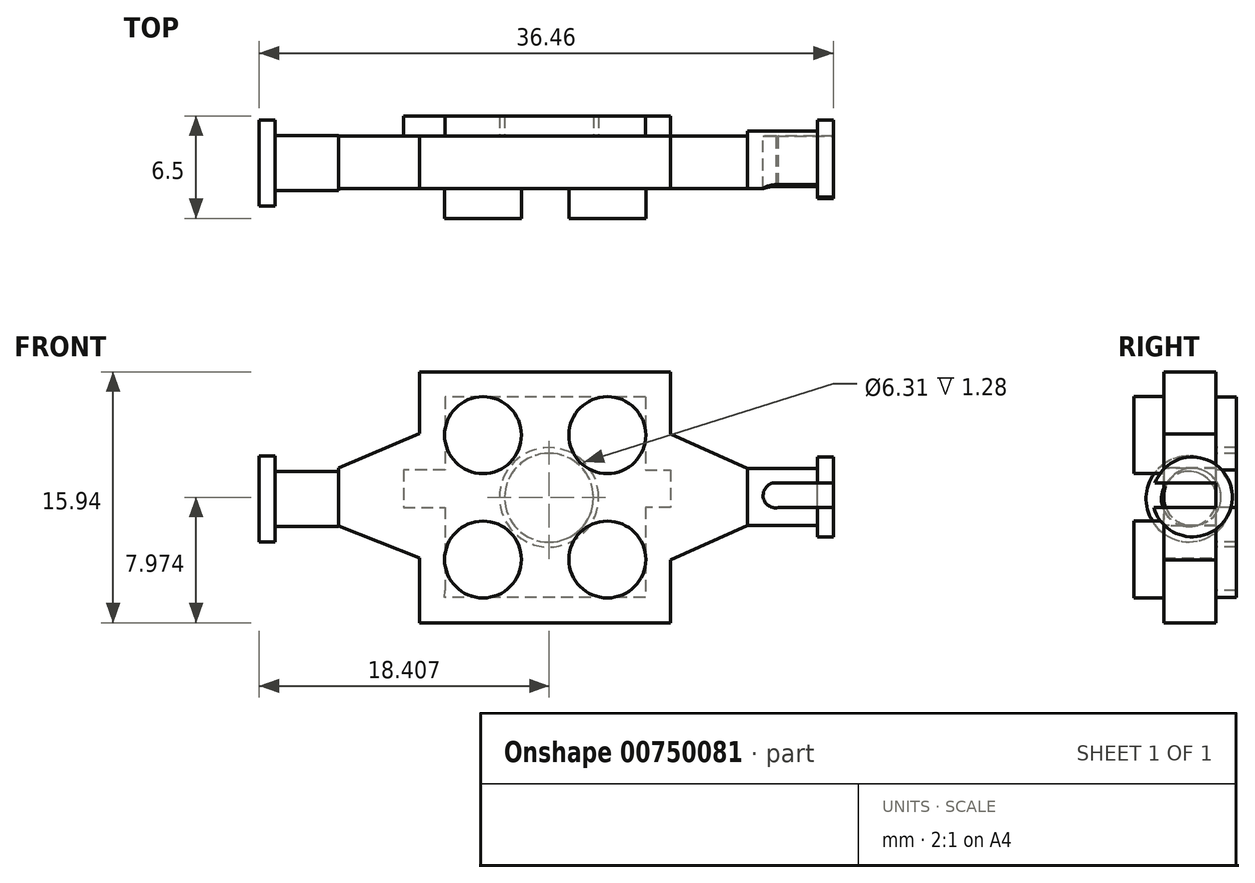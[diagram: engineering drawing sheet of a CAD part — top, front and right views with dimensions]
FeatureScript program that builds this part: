
annotation { "Feature Type Name" : "Feature", "Feature Type Description" : "" }
export const myFeature = defineFeature(function(context is Context, id is Id, definition is map)
    precondition{}
    {
        {
            var Q0;
            Q0=qCreatedBy(makeId("Front.planeOp"),FACE);
            var sketch = newSketch(context, id + "F0", { "sketchPlane" : qUnion([Q0])});
            skLineSegment(sketch, "E0.bottom", {"start": v(-41.3, 42.7) * mm, "end": v(-25.36, 42.7) * mm});
            skLineSegment(sketch, "E0.top", {"start": v(-41.3, 26.75) * mm, "end": v(-25.36, 26.75) * mm});
            skLineSegment(sketch, "E0.left", {"start": v(-41.3, 42.7) * mm, "end": v(-41.3, 26.75) * mm});
            skLineSegment(sketch, "E0.right", {"start": v(-25.36, 42.7) * mm, "end": v(-25.36, 26.75) * mm});
            skSolve(sketch);
        }
        {
            var Q0;
            Q0=makeQuery(id+"F0.imprint","IMPRINT",FACE,{"disambiguationData":[TD([[makeQuery(id+"F0.imprint","IMPRINT",EDGE,{"derivedFrom":sQuery(id+"F0.wireOp",EDGE,"E0.bottom")}),-1.0]])]});
            extrude(context, id + "F1", {"entities" : qUnion([Q0]), "depth" : 3.32 * mm, "offsetDistance" : 25 * mm});
        }
        {
            var Q0;
            Q0=makeQuery(id+"F1.opExtrude","CAP_FACE",FACE,{"disambiguationData":[OSD([sQuery(id+"F0.wireOp",EDGE,"E0.bottom"),sQuery(id+"F0.wireOp",EDGE,"E0.top"),sQuery(id+"F0.wireOp",EDGE,"E0.left"),sQuery(id+"F0.wireOp",EDGE,"E0.right")])],"isStart":false});
            var sketch = newSketch(context, id + "F2", { "sketchPlane" : qUnion([Q0])});
            skCircle(sketch, "E1", {"center": v(-37.28, 38.67) * mm, "radius": 2.44 * mm});
            skCircle(sketch, "E2", {"center": v(-29.38, 38.67) * mm, "radius": 2.44 * mm});
            skCircle(sketch, "E3", {"center": v(-37.28, 30.77) * mm, "radius": 2.44 * mm});
            skCircle(sketch, "E4", {"center": v(-29.38, 30.77) * mm, "radius": 2.44 * mm});
            skLineSegment(sketch, "E5", {"start": v(-26.94, 38.67) * mm, "end": v(-25.36, 38.67) * mm});
            skLineSegment(sketch, "E6", {"start": v(-29.38, 41.11) * mm, "end": v(-29.38, 42.7) * mm});
            skLineSegment(sketch, "E7", {"start": v(-39.72, 38.67) * mm, "end": v(-41.3, 38.67) * mm});
            skLineSegment(sketch, "E8", {"start": v(-37.28, 41.11) * mm, "end": v(-37.28, 42.7) * mm});
            skLineSegment(sketch, "E9", {"start": v(-39.72, 30.77) * mm, "end": v(-41.3, 30.77) * mm});
            skLineSegment(sketch, "E10", {"start": v(-37.28, 28.33) * mm, "end": v(-37.28, 26.75) * mm});
            skLineSegment(sketch, "E11", {"start": v(-29.38, 28.33) * mm, "end": v(-29.38, 26.75) * mm});
            skLineSegment(sketch, "E12", {"start": v(-26.94, 30.77) * mm, "end": v(-25.36, 30.77) * mm});
            skSolve(sketch);
        }
        {
            var Q0;
            Q0 = qSketchRegion(id + "F2", true);
            extrude(context, id + "F3", {"entities" : qUnion([Q0]), "operationType" : NewBodyOperationType.ADD, "depth" : 1.9 * mm, "offsetDistance" : 25 * mm});
        }
        {
            var Q0;
            Q0=makeQuery(id+"F1.opExtrude","CAP_FACE",FACE,{"disambiguationData":[OSD([sQuery(id+"F0.wireOp",EDGE,"E0.bottom"),sQuery(id+"F0.wireOp",EDGE,"E0.top"),sQuery(id+"F0.wireOp",EDGE,"E0.left"),sQuery(id+"F0.wireOp",EDGE,"E0.right")])],"isStart":false});
            var sketch = newSketch(context, id + "F4", { "sketchPlane" : qUnion([Q0])});
            skLineSegment(sketch, "E13", {"start": v(-25.36, 38.73) * mm, "end": v(-20.49, 36.54) * mm});
            skLineSegment(sketch, "E14", {"start": v(-20.49, 36.54) * mm, "end": v(-20.49, 32.95) * mm});
            skLineSegment(sketch, "E15", {"start": v(-20.49, 32.95) * mm, "end": v(-25.36, 30.76) * mm});
            skLineSegment(sketch, "E16", {"start": v(-25.36, 30.76) * mm, "end": v(-25.36, 38.73) * mm});
            skSolve(sketch);
        }
        {
            var Q0;
            Q0 = qSketchRegion(id + "F4", true);
            extrude(context, id + "F5", {"entities" : qUnion([Q0]), "oppositeDirection" : true, "depth" : 3.32 * mm, "offsetDistance" : 25 * mm});
        }
        {
            var Q0;
            Q0=makeQuery(id+"F5.opExtrude","SWEPT_FACE",FACE,{"disambiguationData":[OSD([sQuery(id+"F4.wireOp",EDGE,"E14")])]});
            var sketch = newSketch(context, id + "F6", { "sketchPlane" : qUnion([Q0])});
            skCircle(sketch, "E17", {"center": v(-1.5, 34.75) * mm, "radius": 1.82 * mm});
            skPoint(sketch, "E17.centerSnap0", {"position": v(0, 34.75) * mm});
            skSolve(sketch);
        }
        {
            var Q0;
            Q0 = qSketchRegion(id + "F6", true);
            extrude(context, id + "F7", {"entities" : qUnion([Q0]), "operationType" : NewBodyOperationType.ADD, "depth" : 4.44 * mm, "offsetDistance" : 25 * mm});
        }
        {
            var Q0;
            Q0=makeQuery(id+"F7.opExtrude","CAP_FACE",FACE,{"disambiguationData":[OSD([sQuery(id+"F6.wireOp",EDGE,"E17")])],"isStart":false});
            var sketch = newSketch(context, id + "F8", { "sketchPlane" : qUnion([Q0])});
            skCircle(sketch, "E18", {"center": v(-1.5, 34.75) * mm, "radius": 2.54 * mm});
            skSolve(sketch);
        }
        {
            var Q0;
            Q0 = qSketchRegion(id + "F8", true);
            extrude(context, id + "F9", {"entities" : qUnion([Q0]), "operationType" : NewBodyOperationType.ADD, "depth" : 1.02 * mm, "offsetDistance" : 25 * mm});
        }
        {
            var Q0;
            Q0=qCreatedBy(makeId("Front.planeOp"),FACE);
            var sketch = newSketch(context, id + "F10", { "sketchPlane" : qUnion([Q0])});
            skArc(sketch, "E19", {"start": v(-18.64, 35.65) * mm, "mid": v(-19.49, 34.79) * mm, "end": v(-18.52, 34.07) * mm});
            skLineSegment(sketch, "E20", {"start": v(-18.64, 35.65) * mm, "end": v(-15.04, 35.65) * mm});
            skLineSegment(sketch, "E21", {"start": v(-15.04, 35.65) * mm, "end": v(-15.04, 34.07) * mm});
            skLineSegment(sketch, "E22", {"start": v(-15.04, 34.07) * mm, "end": v(-18.52, 34.07) * mm});
            skLineSegment(sketch, "E23", {"start": v(-15.04, 35.65) * mm, "end": v(-14.8, 35.65) * mm});
            skLineSegment(sketch, "E24", {"start": v(-14.8, 35.65) * mm, "end": v(-14.8, 34.07) * mm});
            skLineSegment(sketch, "E25", {"start": v(-14.8, 34.07) * mm, "end": v(-15.04, 34.07) * mm});
            skSolve(sketch);
        }
        {
            var Q0;
            Q0 = qSketchRegion(id + "F10", true);
            var Q1;
            Q1 = qSketchRegion(id + "FvUQe6Ft84rgAIr_2", true);
            extrude(context, id + "F11", {"entities" : qUnion([Q0, Q1]), "operationType" : NewBodyOperationType.REMOVE, "depth" : 6 * mm, "offsetDistance" : 25 * mm});
        }
        {
            var Q0;
            Q0=makeQuery(id+"F1.opExtrude","CAP_FACE",FACE,{"disambiguationData":[OSD([sQuery(id+"F0.wireOp",EDGE,"E0.bottom"),sQuery(id+"F0.wireOp",EDGE,"E0.top"),sQuery(id+"F0.wireOp",EDGE,"E0.left"),sQuery(id+"F0.wireOp",EDGE,"E0.right")])],"isStart":false});
            var sketch = newSketch(context, id + "F12", { "sketchPlane" : qUnion([Q0])});
            skSolve(sketch);
        }
        {
            var Q0;
            Q0=makeQuery(id+"F12.imprint","IMPRINT",FACE,{"disambiguationData":[TD([[makeQuery(id+"F12.imprint","IMPRINT",EDGE,{"derivedFrom":makeQuery(id+"F1.opExtrude","CAP_EDGE",EDGE,{"disambiguationData":[OSD([sQuery(id+"F0.wireOp",EDGE,"E0.bottom")])],"isStart":false})}),-1.0]])]});
            var sketch = newSketch(context, id + "F13", { "sketchPlane" : qUnion([Q0])});
            skLineSegment(sketch, "E26", {"start": v(-46.45, 32.92) * mm, "end": v(-41.27, 30.85) * mm});
            skLineSegment(sketch, "E27", {"start": v(-41.27, 38.78) * mm, "end": v(-46.45, 36.6) * mm});
            skLineSegment(sketch, "E28", {"start": v(-46.45, 32.92) * mm, "end": v(-46.45, 36.6) * mm});
            skLineSegment(sketch, "E29", {"start": v(-41.27, 38.78) * mm, "end": v(-41.27, 30.85) * mm});
            skSolve(sketch);
        }
        {
            var Q0;
            Q0 = qSketchRegion(id + "F13", true);
            extrude(context, id + "F14", {"entities" : qUnion([Q0]), "operationType" : NewBodyOperationType.ADD, "oppositeDirection" : true, "depth" : 3.32 * mm, "offsetDistance" : 25 * mm});
        }
        {
            var Q0;
            Q0=makeQuery(id+"F14.opExtrude","SWEPT_FACE",FACE,{"disambiguationData":[OSD([sQuery(id+"F13.wireOp",EDGE,"E28")])]});
            var sketch = newSketch(context, id + "F15", { "sketchPlane" : qUnion([Q0])});
            skCircle(sketch, "E30", {"center": v(1.71, 34.62) * mm, "radius": 1.75 * mm});
            skPoint(sketch, "E31.center.orphan", {"position": v(1.71, 34.84) * mm});
            skSolve(sketch);
        }
        {
            var Q0;
            Q0 = qSketchRegion(id + "F15", true);
            extrude(context, id + "F16", {"entities" : qUnion([Q0]), "operationType" : NewBodyOperationType.ADD, "depth" : 4.02 * mm, "offsetDistance" : 25 * mm});
        }
        {
            var Q0;
            Q0=makeQuery(id+"F16.opExtrude","CAP_FACE",FACE,{"disambiguationData":[OSD([sQuery(id+"F15.wireOp",EDGE,"E30")])],"isStart":false});
            var sketch = newSketch(context, id + "F17", { "sketchPlane" : qUnion([Q0])});
            skCircle(sketch, "E32", {"center": v(1.71, 34.62) * mm, "radius": 2.73 * mm});
            skSolve(sketch);
        }
        {
            var Q0;
            Q0 = qSketchRegion(id + "F17", true);
            extrude(context, id + "F18", {"entities" : qUnion([Q0]), "operationType" : NewBodyOperationType.ADD, "depth" : 1.02 * mm, "offsetDistance" : 25 * mm});
        }
        {
            var Q0;
            Q0=makeQuery(id+"F14.boolean.opBoolean","MERGE",FACE,{"derivedFrom":[makeQuery(id+"F1.opExtrude","CAP_FACE",FACE,{"disambiguationData":[OSD([sQuery(id+"F0.wireOp",EDGE,"E0.bottom"),sQuery(id+"F0.wireOp",EDGE,"E0.top"),sQuery(id+"F0.wireOp",EDGE,"E0.left"),sQuery(id+"F0.wireOp",EDGE,"E0.right")])],"isStart":true}),makeQuery(id+"F14.opExtrude","CAP_FACE",FACE,{"disambiguationData":[OSD([sQuery(id+"F13.wireOp",EDGE,"E26"),sQuery(id+"F13.wireOp",EDGE,"E27"),sQuery(id+"F13.wireOp",EDGE,"E28"),sQuery(id+"F13.wireOp",EDGE,"E29")])],"isStart":false})]});
            var sketch = newSketch(context, id + "F19", { "sketchPlane" : qUnion([Q0])});
            skPoint(sketch, "E33.oppositeSnap0", {"position": v(41.3, 28.8) * mm});
            skLineSegment(sketch, "E33.bottom", {"start": v(26.97, 41.08) * mm, "end": v(39.69, 41.08) * mm});
            skLineSegment(sketch, "E33.left", {"start": v(26.97, 41.08) * mm, "end": v(26.97, 36.46) * mm});
            skLineSegment(sketch, "E33.right", {"start": v(39.69, 41.08) * mm, "end": v(39.69, 36.46) * mm});
            skPoint(sketch, "E34.endSnap0", {"position": v(26.97, 35.17) * mm});
            skPoint(sketch, "E34.end.orphan", {"position": v(26.97, 34.95) * mm});
            skPoint(sketch, "E34.start.orphan", {"position": v(25.36, 34.72) * mm});
            skLineSegment(sketch, "E35", {"start": v(26.97, 29.26) * mm, "end": v(26.97, 28.36) * mm});
            skLineSegment(sketch, "E36", {"start": v(26.97, 28.36) * mm, "end": v(39.71, 28.36) * mm});
            skLineSegment(sketch, "E37", {"start": v(39.71, 28.36) * mm, "end": v(39.69, 28.8) * mm});
            skCircle(sketch, "E38", {"center": v(33.08, 34.72) * mm, "radius": 3.15 * mm});
            skCircle(sketch, "E39", {"center": v(33.08, 34.7) * mm, "radius": 2.82 * mm});
            skLineSegment(sketch, "E40", {"start": v(26.97, 36.46) * mm, "end": v(24.32, 36.46) * mm});
            skLineSegment(sketch, "E41", {"start": v(24.32, 36.46) * mm, "end": v(24.32, 34.08) * mm});
            skLineSegment(sketch, "E42", {"start": v(24.32, 34.08) * mm, "end": v(26.97, 34.08) * mm});
            skLineSegment(sketch, "E43", {"start": v(39.69, 36.46) * mm, "end": v(42.34, 36.46) * mm});
            skLineSegment(sketch, "E44", {"start": v(42.34, 36.46) * mm, "end": v(42.34, 34.08) * mm});
            skLineSegment(sketch, "E45", {"start": v(42.34, 34.08) * mm, "end": v(39.69, 34.08) * mm});
            skLineSegment(sketch, "E46.trimOffspring", {"start": v(26.97, 35.17) * mm, "end": v(26.97, 34.95) * mm});
            skLineSegment(sketch, "E47.trimOffspring", {"start": v(26.97, 34.08) * mm, "end": v(26.97, 29.26) * mm});
            skLineSegment(sketch, "E48.trimOffspring", {"start": v(39.69, 34.08) * mm, "end": v(39.69, 28.8) * mm});
            skSolve(sketch);
        }
        {
            var Q0;
            Q0=makeQuery(id+"F19.imprint","IMPRINT",FACE,{"disambiguationData":[TD([[makeQuery(id+"F19.imprint","IMPRINT",EDGE,{"derivedFrom":sQuery(id+"F19.wireOp",EDGE,"E33.bottom")}),-1.0]])]});
            var Q1;
            Q1=makeQuery(id+"F19.imprint","IMPRINT",FACE,{"disambiguationData":[TD([[makeQuery(id+"F19.imprint","IMPRINT",EDGE,{"derivedFrom":sQuery(id+"F19.wireOp",EDGE,"E39")}),1.0]])]});
            extrude(context, id + "F20", {"entities" : qUnion([Q0, Q1]), "operationType" : NewBodyOperationType.ADD, "depth" : 1.28 * mm, "offsetDistance" : 25 * mm});
        }
    });
